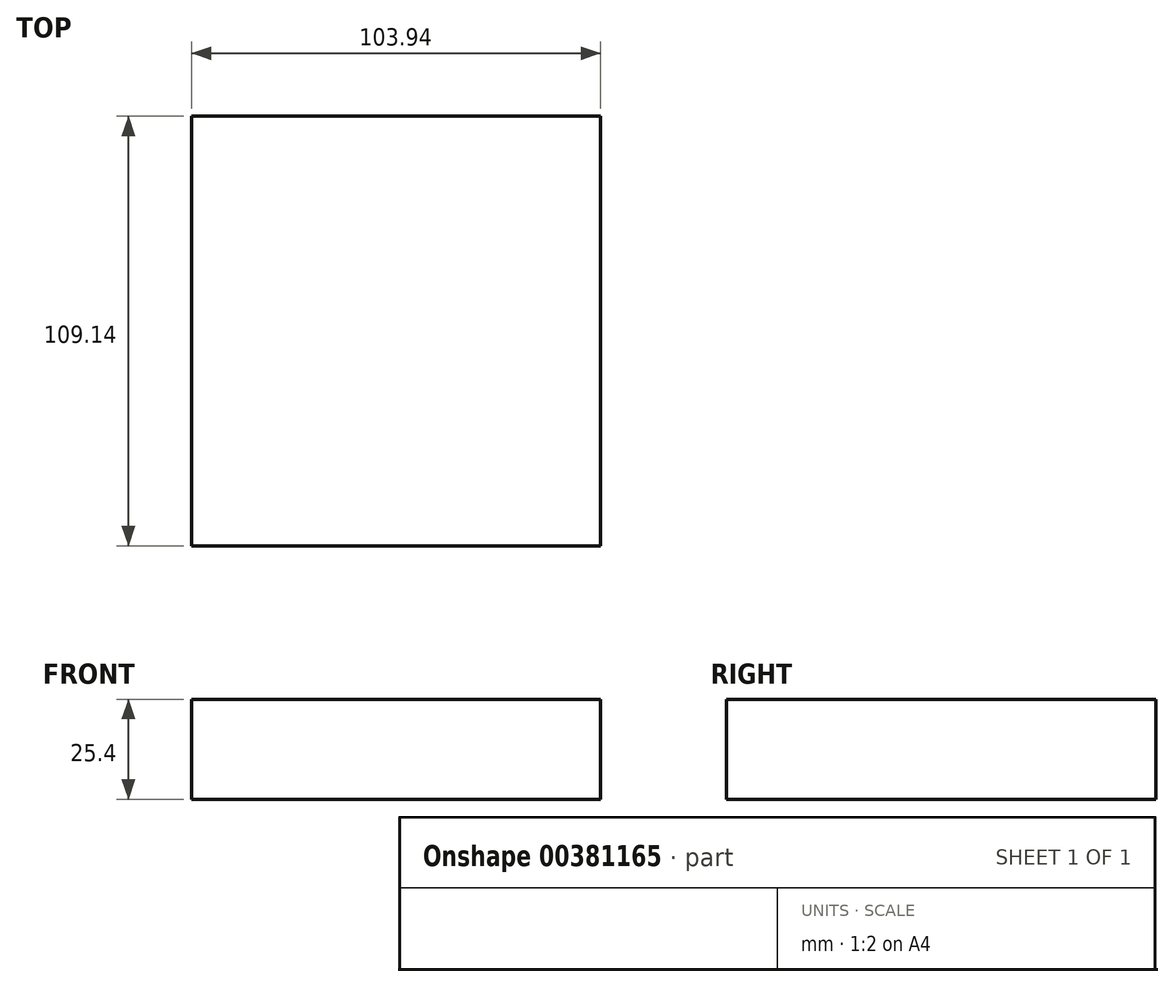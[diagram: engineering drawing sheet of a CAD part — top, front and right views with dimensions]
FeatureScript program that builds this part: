
annotation { "Feature Type Name" : "Feature", "Feature Type Description" : "" }
export const myFeature = defineFeature(function(context is Context, id is Id, definition is map)
    precondition{}
    {
        {
            var Q0;
            Q0=qCreatedBy(makeId("Top.planeOp"),FACE);
            var sketch = newSketch(context, id + "F0", { "sketchPlane" : qUnion([Q0])});
            skLineSegment(sketch, "E0.bottom", {"start": v(51.97, 54.57) * mm, "end": v(-51.97, 54.57) * mm});
            skLineSegment(sketch, "E0.top", {"start": v(51.97, -54.57) * mm, "end": v(-51.97, -54.57) * mm});
            skLineSegment(sketch, "E0.left", {"start": v(51.97, 54.57) * mm, "end": v(51.97, -54.57) * mm});
            skLineSegment(sketch, "E0.right", {"start": v(-51.97, 54.57) * mm, "end": v(-51.97, -54.57) * mm});
            skPoint(sketch, "E0.middle", {"position": v(0, 0) * mm});
            skSolve(sketch);
        }
        {
            var Q0;
            Q0 = qSketchRegion(id + "F0", true);
            extrude(context, id + "F1", {"entities" : qUnion([Q0]), "depth" : 25.4 * mm});
        }
    });
